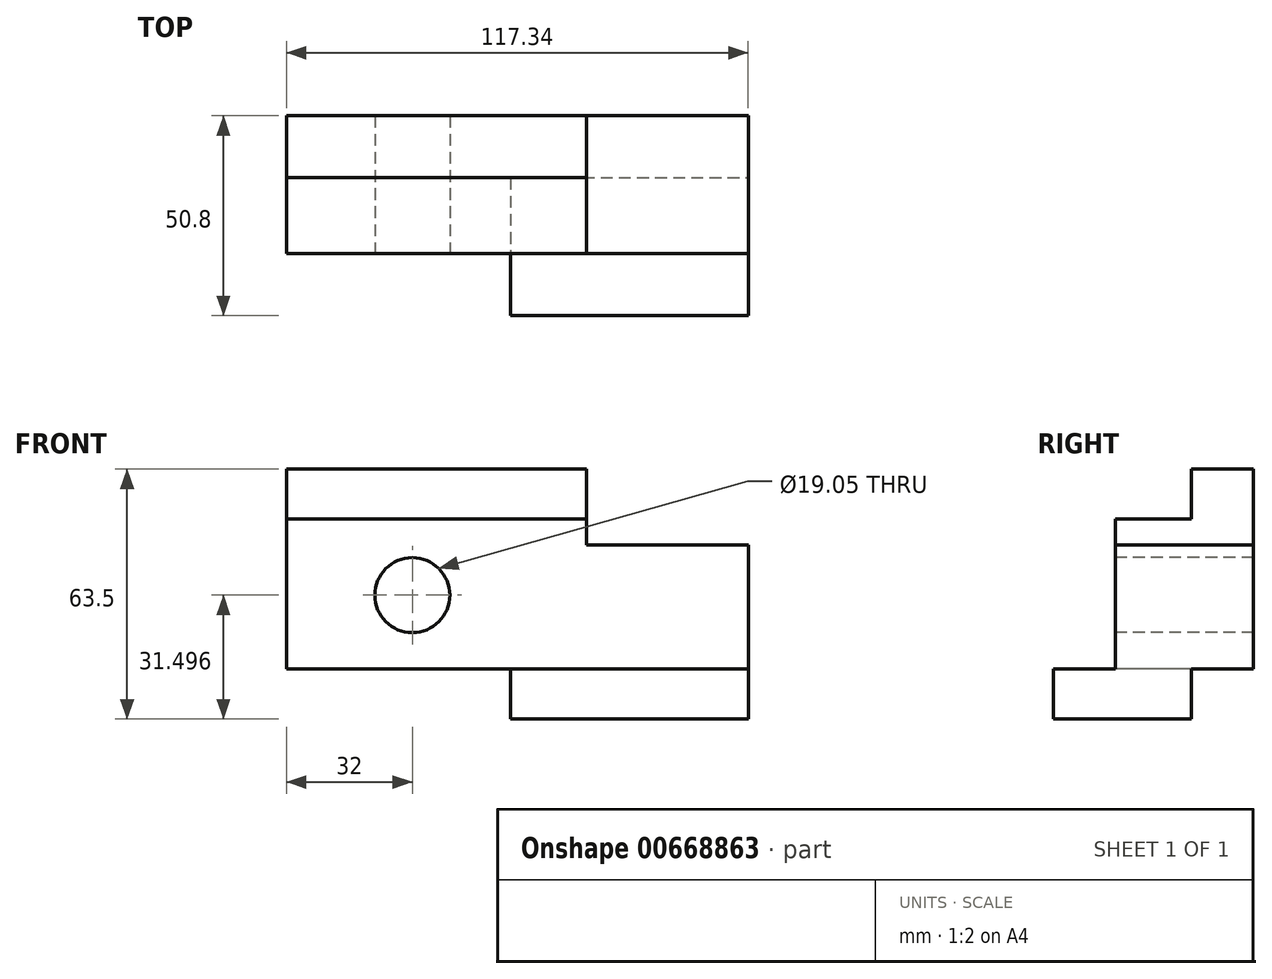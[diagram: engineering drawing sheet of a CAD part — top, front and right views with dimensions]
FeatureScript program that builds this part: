
annotation { "Feature Type Name" : "Feature", "Feature Type Description" : "" }
export const myFeature = defineFeature(function(context is Context, id is Id, definition is map)
    precondition{}
    {
        {
            var Q0;
            Q0=qCreatedBy(makeId("Front.planeOp"),FACE);
            var sketch = newSketch(context, id + "F0", { "sketchPlane" : qUnion([Q0])});
            skLineSegment(sketch, "E0.bottom", {"start": v(-58.67, 31.75) * mm, "end": v(58.67, 31.75) * mm});
            skLineSegment(sketch, "E0.top", {"start": v(-58.67, -31.75) * mm, "end": v(58.67, -31.75) * mm});
            skLineSegment(sketch, "E0.left", {"start": v(-58.67, 31.75) * mm, "end": v(-58.67, -31.75) * mm});
            skLineSegment(sketch, "E0.right", {"start": v(58.67, 31.75) * mm, "end": v(58.67, -31.75) * mm});
            skPoint(sketch, "E0.middle", {"position": v(0, 0) * mm});
            skSolve(sketch);
        }
        {
            var Q0;
            Q0 = qSketchRegion(id + "F0", true);
            extrude(context, id + "F1", {"entities" : qUnion([Q0]), "depth" : 50.8 * mm, "offsetDistance" : 25.4 * mm});
        }
        {
            var Q0;
            Q0=makeQuery(id+"F1.opExtrude","CAP_FACE",FACE,{"disambiguationData":[OSD([sQuery(id+"F0.wireOp",EDGE,"E0.bottom"),sQuery(id+"F0.wireOp",EDGE,"E0.top"),sQuery(id+"F0.wireOp",EDGE,"E0.left"),sQuery(id+"F0.wireOp",EDGE,"E0.right")])],"isStart":false});
            var sketch = newSketch(context, id + "F2", { "sketchPlane" : qUnion([Q0])});
            skLineSegment(sketch, "E1.bottom", {"start": v(58.67, 31.75) * mm, "end": v(17.53, 31.75) * mm});
            skLineSegment(sketch, "E1.top", {"start": v(58.67, 12.45) * mm, "end": v(17.53, 12.45) * mm});
            skLineSegment(sketch, "E1.left", {"start": v(58.67, 31.75) * mm, "end": v(58.67, 12.45) * mm});
            skLineSegment(sketch, "E1.right", {"start": v(17.53, 31.75) * mm, "end": v(17.53, 12.45) * mm});
            skSolve(sketch);
        }
        {
            var Q0;
            Q0 = qSketchRegion(id + "F2", true);
            extrude(context, id + "F3", {"entities" : qUnion([Q0]), "operationType" : NewBodyOperationType.REMOVE, "endBound" : BoundingType.THROUGH_ALL, "oppositeDirection" : true, "depth" : 25.4 * mm, "offsetDistance" : 25.4 * mm});
        }
        {
            var Q0;
            Q0=makeQuery(id+"F1.opExtrude","CAP_FACE",FACE,{"disambiguationData":[OSD([sQuery(id+"F0.wireOp",EDGE,"E0.bottom"),sQuery(id+"F0.wireOp",EDGE,"E0.top"),sQuery(id+"F0.wireOp",EDGE,"E0.left"),sQuery(id+"F0.wireOp",EDGE,"E0.right")])],"isStart":false});
            var sketch = newSketch(context, id + "F4", { "sketchPlane" : qUnion([Q0])});
            skLineSegment(sketch, "E2.bottom", {"start": v(-58.67, -31.75) * mm, "end": v(-1.78, -31.75) * mm});
            skLineSegment(sketch, "E2.top", {"start": v(-58.67, -19.05) * mm, "end": v(-1.78, -19.05) * mm});
            skLineSegment(sketch, "E2.left", {"start": v(-58.67, -31.75) * mm, "end": v(-58.67, -19.05) * mm});
            skLineSegment(sketch, "E2.right", {"start": v(-1.78, -31.75) * mm, "end": v(-1.78, -19.05) * mm});
            skSolve(sketch);
        }
        {
            var Q0;
            Q0=makeQuery(id+"F1.opExtrude","CAP_FACE",FACE,{"disambiguationData":[OSD([sQuery(id+"F0.wireOp",EDGE,"E0.bottom"),sQuery(id+"F0.wireOp",EDGE,"E0.top"),sQuery(id+"F0.wireOp",EDGE,"E0.left"),sQuery(id+"F0.wireOp",EDGE,"E0.right")])],"isStart":false});
            var sketch = newSketch(context, id + "F5", { "sketchPlane" : qUnion([Q0])});
            skCircle(sketch, "E3", {"center": v(-26.67, -0.25) * mm, "radius": 9.53 * mm});
            skSolve(sketch);
        }
        {
            var Q0;
            Q0 = qSketchRegion(id + "F5", true);
            extrude(context, id + "F6", {"entities" : qUnion([Q0]), "operationType" : NewBodyOperationType.REMOVE, "endBound" : BoundingType.THROUGH_ALL, "oppositeDirection" : true, "depth" : 25.4 * mm, "offsetDistance" : 25.4 * mm});
        }
        {
            var Q0;
            Q0=makeQuery(id+"F1.opExtrude","SWEPT_FACE",FACE,{"disambiguationData":[OSD([sQuery(id+"F0.wireOp",EDGE,"E0.right")])]});
            var sketch = newSketch(context, id + "F7", { "sketchPlane" : qUnion([Q0])});
            skLineSegment(sketch, "E4.bottom", {"start": v(0, -31.75) * mm, "end": v(-15.75, -31.75) * mm});
            skLineSegment(sketch, "E4.top", {"start": v(0, -19.05) * mm, "end": v(-15.75, -19.05) * mm});
            skLineSegment(sketch, "E4.left", {"start": v(0, -31.75) * mm, "end": v(0, -19.05) * mm});
            skLineSegment(sketch, "E4.right", {"start": v(-15.75, -31.75) * mm, "end": v(-15.75, -19.05) * mm});
            skSolve(sketch);
        }
        {
            var Q0;
            Q0 = qSketchRegion(id + "F7", true);
            extrude(context, id + "F8", {"entities" : qUnion([Q0]), "operationType" : NewBodyOperationType.REMOVE, "endBound" : BoundingType.THROUGH_ALL, "oppositeDirection" : true, "depth" : 25.4 * mm, "offsetDistance" : 25.4 * mm});
        }
        {
            var Q0;
            Q0=makeQuery(id+"F3.boolean.opBoolean","COPY",FACE,{"derivedFrom":makeQuery(id+"F3.opExtrude","SWEPT_FACE",FACE,{"disambiguationData":[OSD([sQuery(id+"F2.wireOp",EDGE,"E1.right")])]})});
            var sketch = newSketch(context, id + "F9", { "sketchPlane" : qUnion([Q0])});
            skLineSegment(sketch, "E5.bottom", {"start": v(-50.8, 31.75) * mm, "end": v(-15.75, 31.75) * mm});
            skLineSegment(sketch, "E5.top", {"start": v(-50.8, 19.05) * mm, "end": v(-15.75, 19.05) * mm});
            skLineSegment(sketch, "E5.left", {"start": v(-50.8, 31.75) * mm, "end": v(-50.8, 19.05) * mm});
            skLineSegment(sketch, "E5.right", {"start": v(-15.75, 31.75) * mm, "end": v(-15.75, 19.05) * mm});
            skSolve(sketch);
        }
        {
            var Q0;
            Q0 = qSketchRegion(id + "F9", true);
            extrude(context, id + "F10", {"entities" : qUnion([Q0]), "operationType" : NewBodyOperationType.REMOVE, "endBound" : BoundingType.THROUGH_ALL, "oppositeDirection" : true, "depth" : 25.4 * mm, "offsetDistance" : 25.4 * mm});
        }
        {
            var Q0;
            Q0=makeQuery(id+"F3.boolean.opBoolean","COPY",FACE,{"derivedFrom":makeQuery(id+"F3.opExtrude","SWEPT_FACE",FACE,{"disambiguationData":[OSD([sQuery(id+"F2.wireOp",EDGE,"E1.right")])]})});
            var sketch = newSketch(context, id + "F11", { "sketchPlane" : qUnion([Q0])});
            skLineSegment(sketch, "E6.bottom", {"start": v(-50.8, 19.05) * mm, "end": v(-35.05, 19.05) * mm});
            skLineSegment(sketch, "E6.top", {"start": v(-50.8, -19.05) * mm, "end": v(-35.05, -19.05) * mm});
            skLineSegment(sketch, "E6.left", {"start": v(-50.8, 19.05) * mm, "end": v(-50.8, -19.05) * mm});
            skLineSegment(sketch, "E6.right", {"start": v(-35.05, 19.05) * mm, "end": v(-35.05, -19.05) * mm});
            skSolve(sketch);
        }
        {
            var Q0;
            Q0 = qSketchRegion(id + "F4", true);
            extrude(context, id + "F12", {"entities" : qUnion([Q0]), "operationType" : NewBodyOperationType.REMOVE, "endBound" : BoundingType.THROUGH_ALL, "oppositeDirection" : true, "depth" : 25.4 * mm, "offsetDistance" : 25.4 * mm});
        }
        {
            var Q0;
            Q0 = qSketchRegion(id + "F11", true);
            extrude(context, id + "F13", {"entities" : qUnion([Q0]), "operationType" : NewBodyOperationType.REMOVE, "endBound" : BoundingType.THROUGH_ALL, "oppositeDirection" : true, "depth" : 25.4 * mm, "offsetDistance" : 25.4 * mm});
        }
        {
            var Q0;
            Q0=makeQuery(id+"F1.opExtrude","SWEPT_FACE",FACE,{"disambiguationData":[OSD([sQuery(id+"F0.wireOp",EDGE,"E0.right")])]});
            var sketch = newSketch(context, id + "F14", { "sketchPlane" : qUnion([Q0])});
            skLineSegment(sketch, "E7.bottom", {"start": v(-50.8, 12.45) * mm, "end": v(-35.05, 12.45) * mm});
            skLineSegment(sketch, "E7.top", {"start": v(-50.8, -19.05) * mm, "end": v(-35.05, -19.05) * mm});
            skLineSegment(sketch, "E7.left", {"start": v(-50.8, 12.45) * mm, "end": v(-50.8, -19.05) * mm});
            skLineSegment(sketch, "E7.right", {"start": v(-35.05, 12.45) * mm, "end": v(-35.05, -19.05) * mm});
            skSolve(sketch);
        }
        {
            var Q0;
            Q0 = qSketchRegion(id + "F14", true);
            extrude(context, id + "F15", {"entities" : qUnion([Q0]), "operationType" : NewBodyOperationType.REMOVE, "endBound" : BoundingType.THROUGH_ALL, "oppositeDirection" : true, "depth" : 25.4 * mm, "offsetDistance" : 25.4 * mm});
        }
    });
